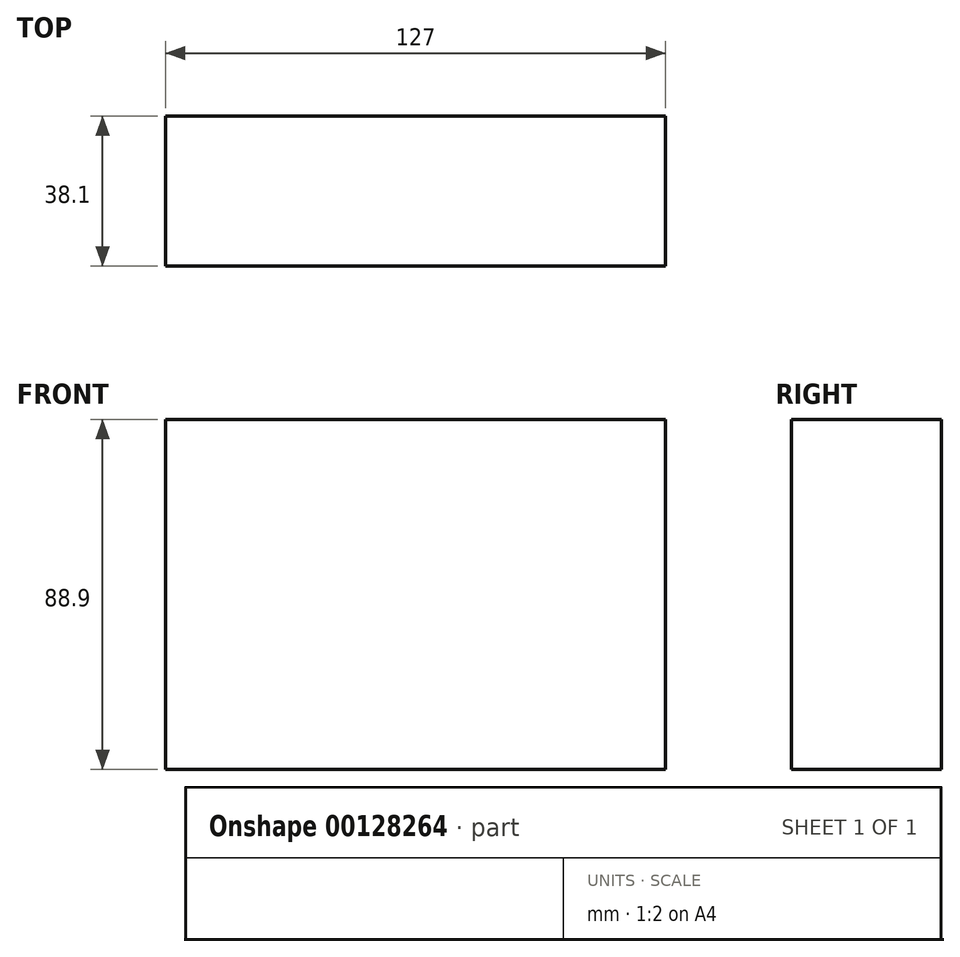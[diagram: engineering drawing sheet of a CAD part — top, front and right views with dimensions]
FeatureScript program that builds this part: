
annotation { "Feature Type Name" : "Feature", "Feature Type Description" : "" }
export const myFeature = defineFeature(function(context is Context, id is Id, definition is map)
    precondition{}
    {
        {
            var Q0;
            Q0=qCreatedBy(makeId("Top.planeOp"),FACE);
            var sketch = newSketch(context, id + "F0", { "sketchPlane" : qUnion([Q0])});
            skLineSegment(sketch, "E0.bottom", {"start": v(63.5, -16.1) * mm, "end": v(-63.5, -16.1) * mm});
            skLineSegment(sketch, "E0.top", {"start": v(63.5, 22) * mm, "end": v(-63.5, 22) * mm});
            skLineSegment(sketch, "E0.left", {"start": v(63.5, -16.1) * mm, "end": v(63.5, 22) * mm});
            skLineSegment(sketch, "E0.right", {"start": v(-63.5, -16.1) * mm, "end": v(-63.5, 22) * mm});
            skPoint(sketch, "E0.middle", {"position": v(0, 2.95) * mm});
            skSolve(sketch);
        }
        {
            var Q0;
            Q0=makeQuery(id+"F0.imprint","IMPRINT",FACE,{"disambiguationData":[TD([[makeQuery(id+"F0.imprint","IMPRINT",EDGE,{"derivedFrom":sQuery(id+"F0.wireOp",EDGE,"E0.bottom")}),-1.0]])]});
            extrude(context, id + "F1", {"entities" : qUnion([Q0]), "depth" : 88.9 * mm, "offsetDistance" : 25.4 * mm});
        }
    });
